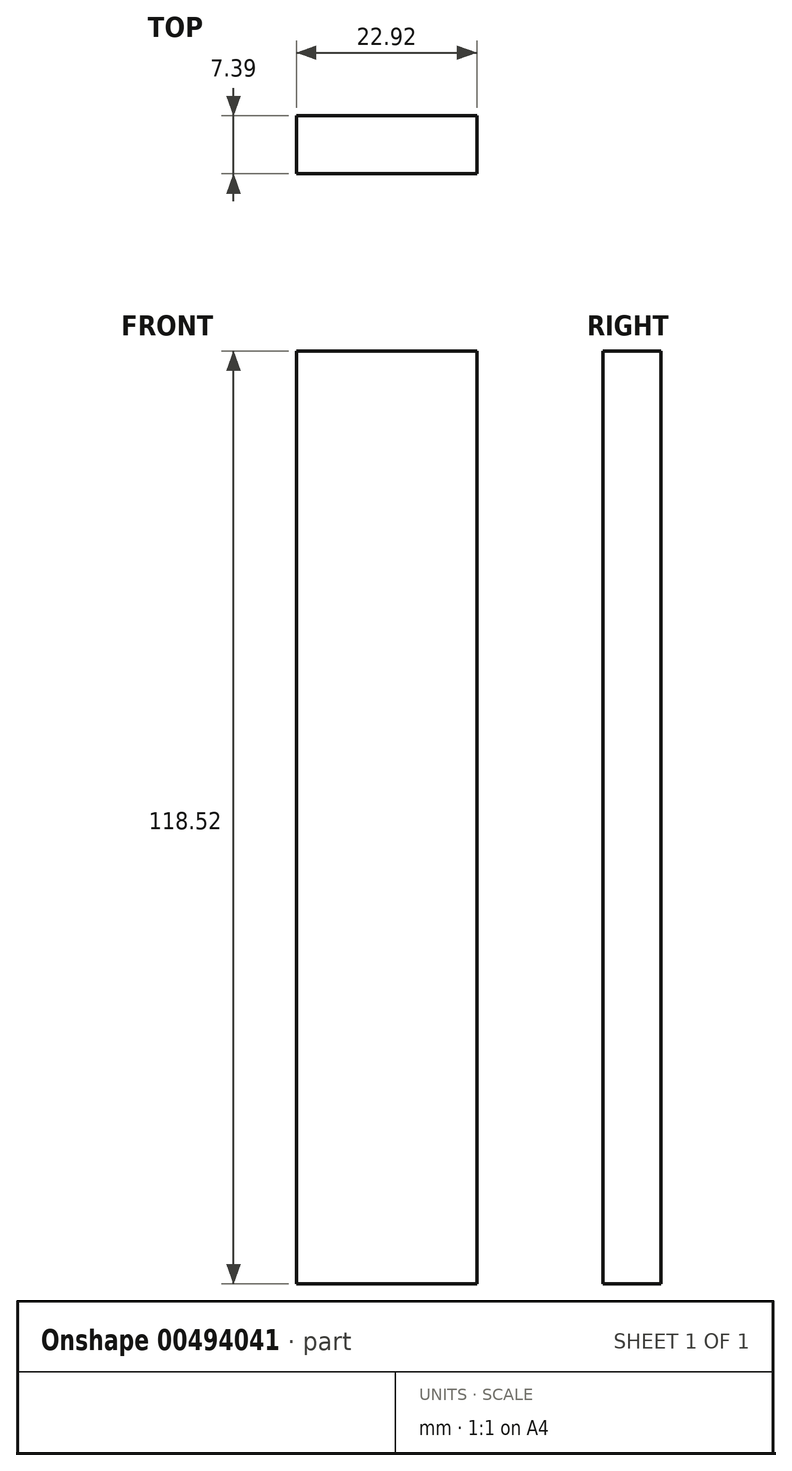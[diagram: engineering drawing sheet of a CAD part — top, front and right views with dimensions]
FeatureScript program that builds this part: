
annotation { "Feature Type Name" : "Feature", "Feature Type Description" : "" }
export const myFeature = defineFeature(function(context is Context, id is Id, definition is map)
    precondition{}
    {
        {
            var Q0;
            Q0=qCreatedBy(makeId("Front.planeOp"),FACE);
            var sketch = newSketch(context, id + "F0", { "sketchPlane" : qUnion([Q0])});
            skLineSegment(sketch, "E0.bottom", {"start": v(-11.46, 59.26) * mm, "end": v(11.46, 59.26) * mm});
            skLineSegment(sketch, "E0.top", {"start": v(-11.46, -59.26) * mm, "end": v(11.46, -59.26) * mm});
            skLineSegment(sketch, "E0.left", {"start": v(-11.46, 59.26) * mm, "end": v(-11.46, -59.26) * mm});
            skLineSegment(sketch, "E0.right", {"start": v(11.46, 59.26) * mm, "end": v(11.46, -59.26) * mm});
            skPoint(sketch, "E0.middle", {"position": v(0, 0) * mm});
            skSolve(sketch);
        }
        {
            var Q0;
            Q0=makeQuery(id+"F0.imprint","IMPRINT",FACE,{"disambiguationData":[TD([[makeQuery(id+"F0.imprint","IMPRINT",EDGE,{"derivedFrom":sQuery(id+"F0.wireOp",EDGE,"E0.bottom")}),-1.0]])]});
            extrude(context, id + "F1", {"entities" : qUnion([Q0]), "depth" : 7.39 * mm});
        }
    });
